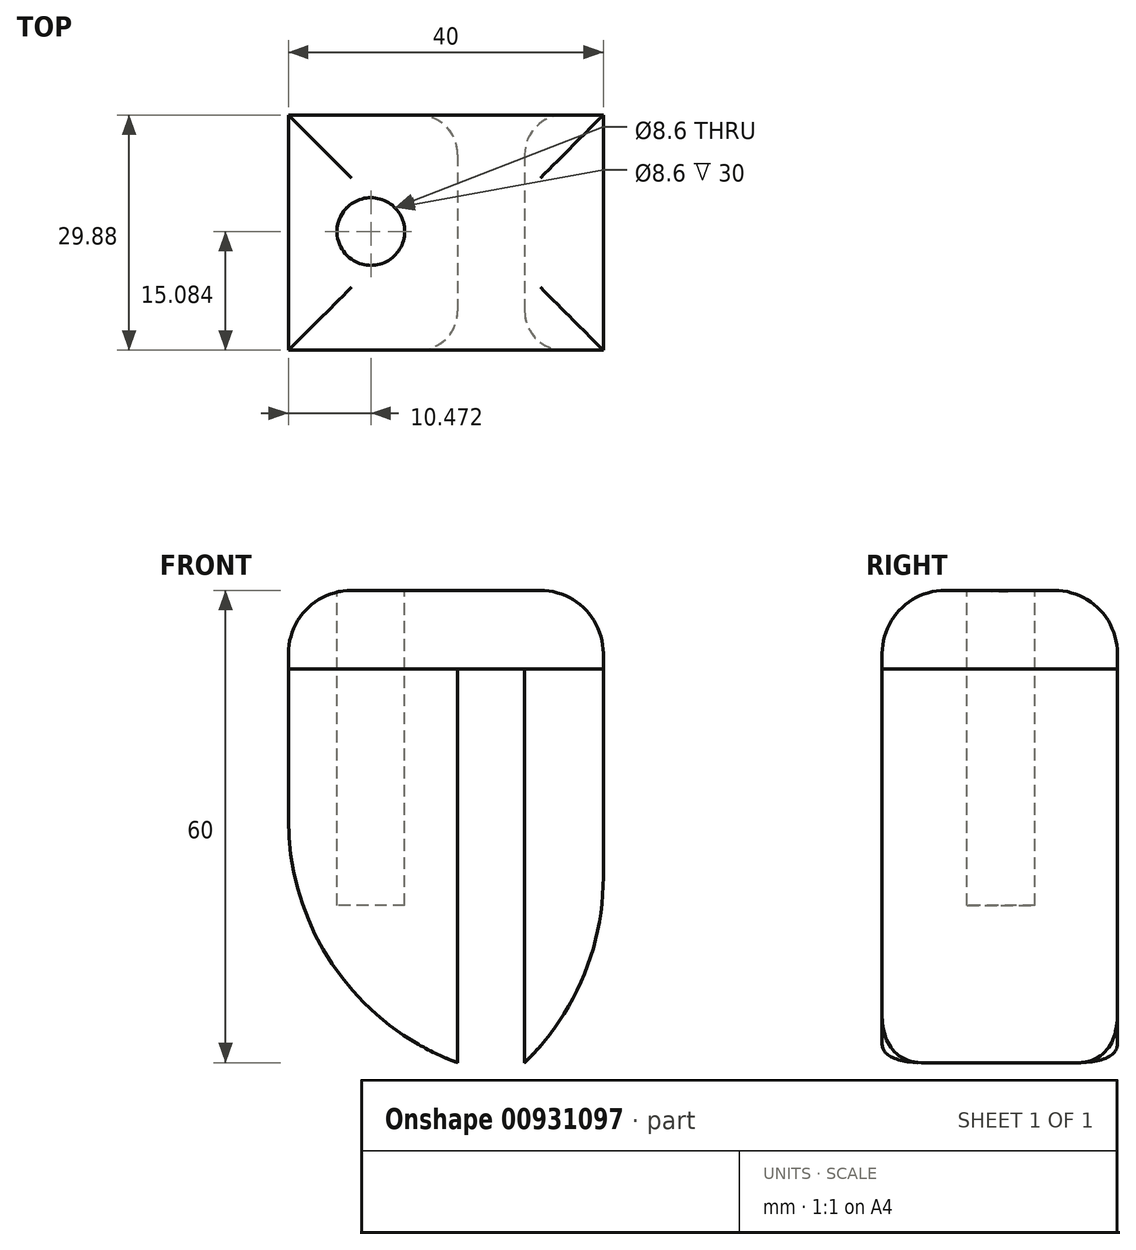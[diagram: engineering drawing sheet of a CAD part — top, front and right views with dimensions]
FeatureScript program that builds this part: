
annotation { "Feature Type Name" : "Feature", "Feature Type Description" : "" }
export const myFeature = defineFeature(function(context is Context, id is Id, definition is map)
    precondition{}
    {
        {
            var Q0;
            Q0=qCreatedBy(makeId("Top.planeOp"),FACE);
            var sketch = newSketch(context, id + "F0", { "sketchPlane" : qUnion([Q0])});
            skLineSegment(sketch, "E0.bottom", {"start": v(-40, 0) * mm, "end": v(0, 0) * mm});
            skLineSegment(sketch, "E0.top", {"start": v(-40, 29.88) * mm, "end": v(0, 29.88) * mm});
            skLineSegment(sketch, "E0.left", {"start": v(-40, 0) * mm, "end": v(-40, 29.88) * mm});
            skLineSegment(sketch, "E0.right", {"start": v(0, 0) * mm, "end": v(0, 29.88) * mm});
            skLineSegment(sketch, "E1.bottom", {"start": v(0, 29.88) * mm, "end": v(-10, 29.88) * mm});
            skLineSegment(sketch, "E1.top", {"start": v(0, 0) * mm, "end": v(-10, 0) * mm});
            skLineSegment(sketch, "E1.left", {"start": v(0, 29.88) * mm, "end": v(0, 0) * mm});
            skLineSegment(sketch, "E1.right", {"start": v(-10, 29.88) * mm, "end": v(-10, 0) * mm});
            skLineSegment(sketch, "E2.bottom", {"start": v(-18.5, 29.88) * mm, "end": v(-10, 29.88) * mm});
            skLineSegment(sketch, "E2.top", {"start": v(-18.5, 0) * mm, "end": v(-10, 0) * mm});
            skLineSegment(sketch, "E2.left", {"start": v(-18.5, 29.88) * mm, "end": v(-18.5, 0) * mm});
            skSolve(sketch);
        }
        {
            var Q0;
            {var subQ2=sQuery(id+"F0.wireOp",EDGE,"E0.right");Q0=makeQuery(id+"F0.imprint","IMPRINT",FACE,{"disambiguationData":[TD([[makeQuery(id+"F0.imprint","IMPRINT",EDGE,{"derivedFrom":subQ2}),1.0]])]});}
            var Q1;
            {var subQ0=sQuery(id+"F0.wireOp",EDGE,"E0.left");Q1=makeQuery(id+"F0.imprint","IMPRINT",FACE,{"disambiguationData":[TD([[makeQuery(id+"F0.imprint","IMPRINT",EDGE,{"derivedFrom":subQ0}),-1.0]])]});}
            extrude(context, id + "F1", {"entities" : qUnion([Q0, Q1]), "depth" : 50 * mm, "offsetDistance" : 25 * mm});
        }
        {
            var Q0;
            Q0=makeQuery(id+"F1.opExtrude","CAP_FACE",FACE,{"disambiguationData":[OSD([sQuery(id+"F0.wireOp",EDGE,"E0.bottom"),sQuery(id+"F0.wireOp",EDGE,"E0.top"),sQuery(id+"F0.wireOp",EDGE,"E0.left"),sQuery(id+"F0.wireOp",EDGE,"E2.left")])],"isStart":false});
            var sketch = newSketch(context, id + "F2", { "sketchPlane" : qUnion([Q0])});
            skLineSegment(sketch, "E3.bottom", {"start": v(-40, 29.88) * mm, "end": v(0, 29.88) * mm});
            skLineSegment(sketch, "E3.top", {"start": v(-40, 0) * mm, "end": v(0, 0) * mm});
            skLineSegment(sketch, "E3.left", {"start": v(-40, 29.88) * mm, "end": v(-40, 0) * mm});
            skLineSegment(sketch, "E3.right", {"start": v(0, 29.88) * mm, "end": v(0, 0) * mm});
            skSolve(sketch);
        }
        {
            var Q0;
            Q0 = qSketchRegion(id + "F2", true);
            extrude(context, id + "F3", {"entities" : qUnion([Q0]), "depth" : 10 * mm, "offsetDistance" : 25 * mm});
        }
        {
            var Q0;
            Q0=makeQuery(id+"F3.opExtrude","CAP_FACE",FACE,{"disambiguationData":[OSD([sQuery(id+"F2.wireOp",EDGE,"E3.bottom"),sQuery(id+"F2.wireOp",EDGE,"E3.top"),sQuery(id+"F2.wireOp",EDGE,"E3.left"),sQuery(id+"F2.wireOp",EDGE,"E3.right")])],"isStart":false});
            var sketch = newSketch(context, id + "F4", { "sketchPlane" : qUnion([Q0])});
            skCircle(sketch, "E4", {"center": v(-29.53, 15.08) * mm, "radius": 4.3 * mm});
            skSolve(sketch);
        }
        {
            var Q0;
            Q0=makeQuery(id+"F4.imprint","IMPRINT",FACE,{"disambiguationData":[TD([[makeQuery(id+"F4.imprint","IMPRINT",EDGE,{"derivedFrom":sQuery(id+"F4.wireOp",EDGE,"E4")}),1.0]])]});
            extrude(context, id + "F5", {"entities" : qUnion([Q0]), "operationType" : NewBodyOperationType.REMOVE, "oppositeDirection" : true, "depth" : 40 * mm, "offsetDistance" : 25 * mm});
        }
        {
            var Q0;
            Q0=makeQuery(id+"F1.opExtrude","SWEPT_EDGE",EDGE,{"disambiguationData":[OSD([sQuery(id+"F0.wireOp",EDGE,"E0.bottom"),sQuery(id+"F0.wireOp",EDGE,"E2.left")])]});
            var Q1;
            Q1=makeQuery(id+"FTZUa9gHylwExco_3.opFillet","BLEND_EDGE",EDGE,{"blendedFrom":[makeQuery(id+"F1.opExtrude","CAP_EDGE",EDGE,{"disambiguationData":[OSD([sQuery(id+"F0.wireOp",EDGE,"E0.left")])],"isStart":true}),makeQuery(id+"F1.opExtrude","SWEPT_FACE",FACE,{"disambiguationData":[OSD([sQuery(id+"F0.wireOp",EDGE,"E0.bottom")])]})],"blendedInto":[makeQuery(id+"F1.opExtrude","SWEPT_FACE",FACE,{"disambiguationData":[OSD([sQuery(id+"F0.wireOp",EDGE,"E0.bottom")])]})]});
            var Q2;
            Q2=makeQuery(id+"F1.opExtrude","SWEPT_EDGE",EDGE,{"disambiguationData":[OSD([sQuery(id+"F0.wireOp",EDGE,"E0.bottom"),sQuery(id+"F0.wireOp",EDGE,"E1.right")])]});
            fillet(context, id + "F6", {"entities" : qUnion([Q0, Q1, Q2]), "radius" : 5 * mm, "tangentPropagation" : true, "allowEdgeOverflow" : false});
        }
        {
            var Q0;
            Q0=makeQuery(id+"F3.opExtrude","CAP_EDGE",EDGE,{"disambiguationData":[OSD([sQuery(id+"F2.wireOp",EDGE,"E3.left")])],"isStart":false});
            var Q1;
            Q1=makeQuery(id+"F3.opExtrude","CAP_EDGE",EDGE,{"disambiguationData":[OSD([sQuery(id+"F2.wireOp",EDGE,"E3.bottom")])],"isStart":false});
            var Q2;
            Q2=makeQuery(id+"F3.opExtrude","CAP_EDGE",EDGE,{"disambiguationData":[OSD([sQuery(id+"F2.wireOp",EDGE,"E3.top")])],"isStart":false});
            var Q3;
            Q3=makeQuery(id+"F3.opExtrude","CAP_EDGE",EDGE,{"disambiguationData":[OSD([sQuery(id+"F2.wireOp",EDGE,"E3.right")])],"isStart":false});
            fillet(context, id + "F7", {"entities" : qUnion([Q0, Q1, Q2, Q3]), "radius" : 8 * mm, "tangentPropagation" : true, "allowEdgeOverflow" : false});
        }
        {
            var Q0;
            Q0=makeQuery(id+"F1.opExtrude","SWEPT_EDGE",EDGE,{"disambiguationData":[OSD([sQuery(id+"F0.wireOp",EDGE,"E0.top"),sQuery(id+"F0.wireOp",EDGE,"E1.right")])]});
            var Q1;
            Q1=makeQuery(id+"F1.opExtrude","SWEPT_EDGE",EDGE,{"disambiguationData":[OSD([sQuery(id+"F0.wireOp",EDGE,"E0.top"),sQuery(id+"F0.wireOp",EDGE,"E2.left")])]});
            var Q2;
            Q2=makeQuery(id+"FTZUa9gHylwExco_3.opFillet","BLEND_EDGE",EDGE,{"blendedFrom":[makeQuery(id+"F1.opExtrude","CAP_EDGE",EDGE,{"disambiguationData":[OSD([sQuery(id+"F0.wireOp",EDGE,"E0.left")])],"isStart":true}),makeQuery(id+"F1.opExtrude","SWEPT_FACE",FACE,{"disambiguationData":[OSD([sQuery(id+"F0.wireOp",EDGE,"E0.top")])]})],"blendedInto":[makeQuery(id+"F1.opExtrude","SWEPT_FACE",FACE,{"disambiguationData":[OSD([sQuery(id+"F0.wireOp",EDGE,"E0.top")])]})]});
            fillet(context, id + "F8", {"entities" : qUnion([Q0, Q1, Q2]), "radius" : 5 * mm, "tangentPropagation" : true, "allowEdgeOverflow" : false});
        }
        {
            var Q0;
            Q0=makeQuery(id+"F1.opExtrude","CAP_EDGE",EDGE,{"disambiguationData":[OSD([sQuery(id+"F0.wireOp",EDGE,"E0.left")])],"isStart":true});
            var Q1;
            Q1=makeQuery(id+"F1.opExtrude","CAP_EDGE",EDGE,{"disambiguationData":[OSD([sQuery(id+"F0.wireOp",EDGE,"E0.right")])],"isStart":true});
            fillet(context, id + "F9", {"entities" : qUnion([Q0, Q1]), "radius" : 32.83 * mm, "tangentPropagation" : true, "allowEdgeOverflow" : false});
        }
    });
